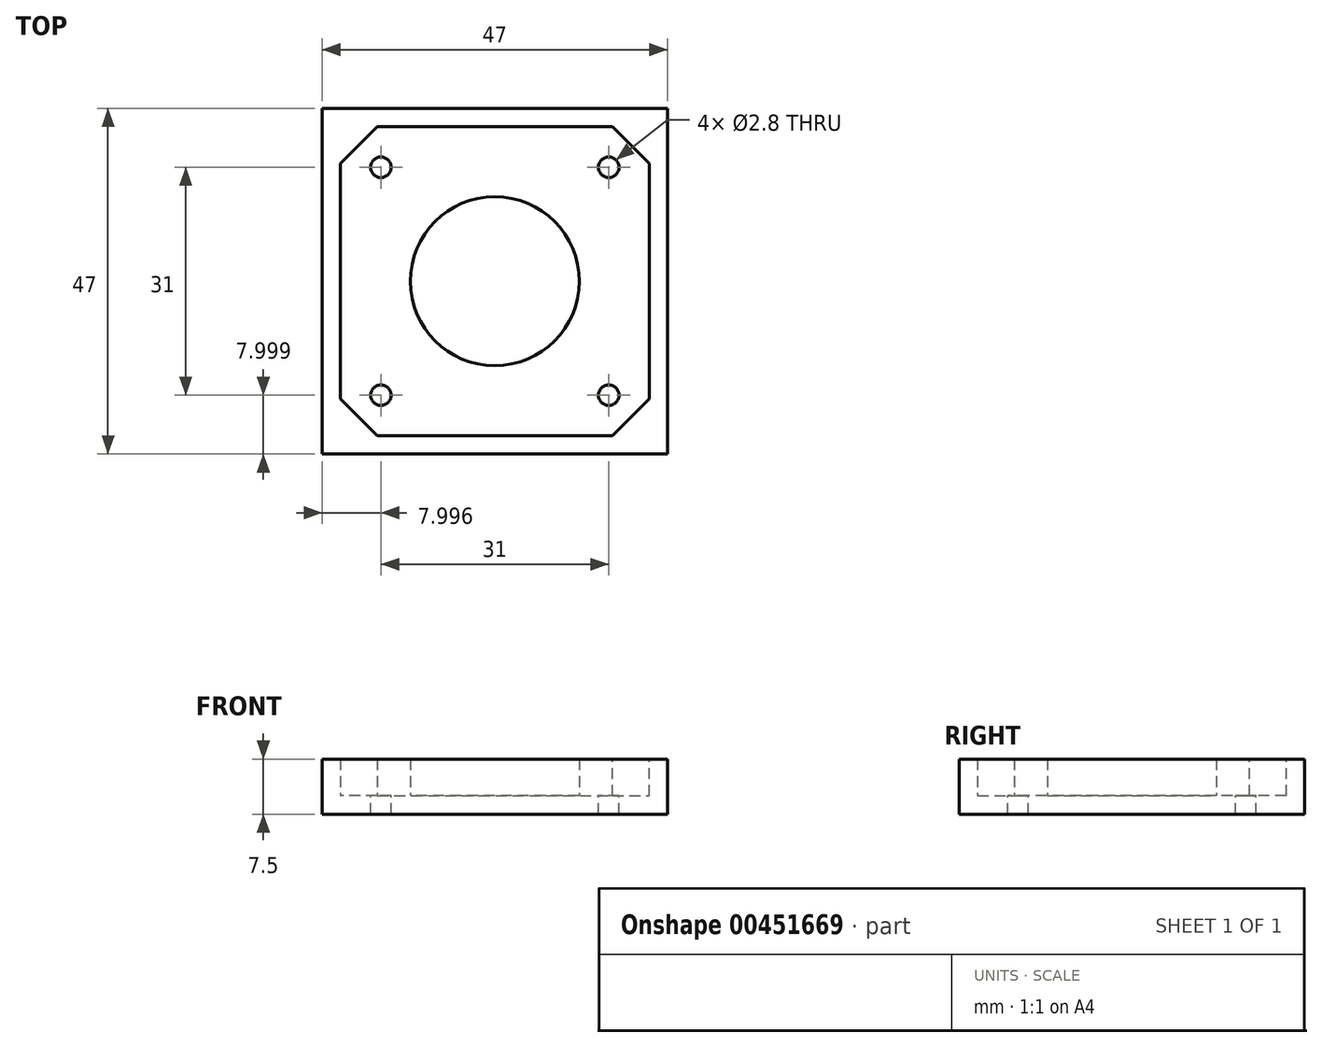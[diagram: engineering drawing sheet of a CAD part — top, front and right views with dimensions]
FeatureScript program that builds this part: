
annotation { "Feature Type Name" : "Feature", "Feature Type Description" : "" }
export const myFeature = defineFeature(function(context is Context, id is Id, definition is map)
    precondition{}
    {
        {
            var Q0;
            Q0=qCreatedBy(makeId("Top.planeOp"),FACE);
            var sketch = newSketch(context, id + "F0", { "sketchPlane" : qUnion([Q0])});
            skLineSegment(sketch, "E0.bottom", {"start": v(-41.82, 29.14) * mm, "end": v(0.18, 29.14) * mm});
            skLineSegment(sketch, "E0.top", {"start": v(-41.82, -12.86) * mm, "end": v(0.18, -12.86) * mm});
            skLineSegment(sketch, "E0.left", {"start": v(-41.82, 29.14) * mm, "end": v(-41.82, -12.86) * mm});
            skLineSegment(sketch, "E0.right", {"start": v(0.18, 29.14) * mm, "end": v(0.18, -12.86) * mm});
            skLineSegment(sketch, "E1", {"start": v(-41.82, 29.14) * mm, "end": v(0.18, -12.86) * mm, "construction": true});
            skCircle(sketch, "E2", {"center": v(-20.82, 8.14) * mm, "radius": 11.5 * mm});
            skLineSegment(sketch, "E3.bottom", {"start": v(-36.32, -7.36) * mm, "end": v(-5.32, -7.36) * mm, "construction": true});
            skLineSegment(sketch, "E3.top", {"start": v(-36.32, 23.64) * mm, "end": v(-5.32, 23.64) * mm, "construction": true});
            skLineSegment(sketch, "E3.left", {"start": v(-36.32, -7.36) * mm, "end": v(-36.32, 23.64) * mm, "construction": true});
            skLineSegment(sketch, "E3.right", {"start": v(-5.32, -7.36) * mm, "end": v(-5.32, 23.64) * mm, "construction": true});
            skCircle(sketch, "E4", {"center": v(-36.32, 23.64) * mm, "radius": 1.4 * mm});
            skCircle(sketch, "E5", {"center": v(-5.32, 23.64) * mm, "radius": 1.4 * mm});
            skCircle(sketch, "E6", {"center": v(-5.32, -7.36) * mm, "radius": 1.4 * mm});
            skCircle(sketch, "E7", {"center": v(-36.32, -7.36) * mm, "radius": 1.4 * mm});
            skSolve(sketch);
        }
        {
            var Q0;
            Q0=makeQuery(id+"F0.imprint","IMPRINT",FACE,{"disambiguationData":[TD([[makeQuery(id+"F0.imprint","IMPRINT",EDGE,{"derivedFrom":sQuery(id+"F0.wireOp",EDGE,"E2")}),1.0]])]});
            var Q1;
            Q1=makeQuery(id+"F0.imprint","IMPRINT",FACE,{"disambiguationData":[TD([[makeQuery(id+"F0.imprint","IMPRINT",EDGE,{"derivedFrom":sQuery(id+"F0.wireOp",EDGE,"E4")}),1.0]])]});
            var Q2;
            Q2=makeQuery(id+"F0.imprint","IMPRINT",FACE,{"disambiguationData":[TD([[makeQuery(id+"F0.imprint","IMPRINT",EDGE,{"derivedFrom":sQuery(id+"F0.wireOp",EDGE,"E5")}),1.0]])]});
            var Q3;
            Q3=makeQuery(id+"F0.imprint","IMPRINT",FACE,{"disambiguationData":[TD([[makeQuery(id+"F0.imprint","IMPRINT",EDGE,{"derivedFrom":sQuery(id+"F0.wireOp",EDGE,"E6")}),1.0]])]});
            var Q4;
            Q4=makeQuery(id+"F0.imprint","IMPRINT",FACE,{"disambiguationData":[TD([[makeQuery(id+"F0.imprint","IMPRINT",EDGE,{"derivedFrom":sQuery(id+"F0.wireOp",EDGE,"E7")}),1.0]])]});
            var Q5;
            Q5=makeQuery(id+"F0.imprint","IMPRINT",FACE,{"disambiguationData":[TD([[makeQuery(id+"F0.imprint","IMPRINT",EDGE,{"derivedFrom":sQuery(id+"F0.wireOp",EDGE,"E0.bottom")}),-1.0]])]});
            extrude(context, id + "F1", {"entities" : qUnion([Q0, Q1, Q2, Q3, Q4, Q5]), "depth" : 5 * mm});
        }
        {
            var Q0;
            Q0=makeQuery(id+"F1.opExtrude","CAP_FACE",FACE,{"disambiguationData":[OSD([sQuery(id+"F0.wireOp",EDGE,"E0.bottom"),sQuery(id+"F0.wireOp",EDGE,"E0.top"),sQuery(id+"F0.wireOp",EDGE,"E0.left"),sQuery(id+"F0.wireOp",EDGE,"E0.right"),sQuery(id+"F0.wireOp",EDGE,"E4"),sQuery(id+"F0.wireOp",EDGE,"E5"),sQuery(id+"F0.wireOp",EDGE,"E6"),sQuery(id+"F0.wireOp",EDGE,"E7")])],"isStart":false});
            shell(context, id + "F2", {"entities" : qUnion([Q0]), "thickness" : 2.5 * mm, "oppositeDirection" : true});
        }
        {
            var Q0;
            Q0=makeQuery(id+"F2.opShell","OFFSET_EDGE",EDGE,{"disambiguationData":[OSD([sQuery(id+"F0.wireOp",EDGE,"E0.bottom"),sQuery(id+"F0.wireOp",EDGE,"E0.left")])]});
            var Q1;
            Q1=makeQuery(id+"F2.opShell","OFFSET_EDGE",EDGE,{"disambiguationData":[OSD([sQuery(id+"F0.wireOp",EDGE,"E0.bottom"),sQuery(id+"F0.wireOp",EDGE,"E0.right")])]});
            var Q2;
            Q2=makeQuery(id+"F2.opShell","OFFSET_EDGE",EDGE,{"disambiguationData":[OSD([sQuery(id+"F0.wireOp",EDGE,"E0.top"),sQuery(id+"F0.wireOp",EDGE,"E0.right")])]});
            var Q3;
            Q3=makeQuery(id+"F2.opShell","OFFSET_EDGE",EDGE,{"disambiguationData":[OSD([sQuery(id+"F0.wireOp",EDGE,"E0.top"),sQuery(id+"F0.wireOp",EDGE,"E0.left")])]});
            chamfer(context, id + "F3", {"entities" : qUnion([Q0, Q1, Q2, Q3]), "width" : 5 * mm, "tangentPropagation" : true});
        }
        {
            var Q0;
            Q0=makeQuery(id+"F0.imprint","IMPRINT",FACE,{"disambiguationData":[TD([[makeQuery(id+"F0.imprint","IMPRINT",EDGE,{"derivedFrom":sQuery(id+"F0.wireOp",EDGE,"E2")}),1.0]])]});
            extrude(context, id + "F4", {"entities" : qUnion([Q0]), "operationType" : NewBodyOperationType.ADD, "depth" : 5 * mm});
        }
        {
            var Q0;
            Q0=makeQuery(id+"F0.imprint","IMPRINT",FACE,{"disambiguationData":[TD([[makeQuery(id+"F0.imprint","IMPRINT",EDGE,{"derivedFrom":sQuery(id+"F0.wireOp",EDGE,"E7")}),1.0]])]});
            var Q1;
            Q1=makeQuery(id+"F0.imprint","IMPRINT",FACE,{"disambiguationData":[TD([[makeQuery(id+"F0.imprint","IMPRINT",EDGE,{"derivedFrom":sQuery(id+"F0.wireOp",EDGE,"E4")}),1.0]])]});
            var Q2;
            Q2=makeQuery(id+"F0.imprint","IMPRINT",FACE,{"disambiguationData":[TD([[makeQuery(id+"F0.imprint","IMPRINT",EDGE,{"derivedFrom":sQuery(id+"F0.wireOp",EDGE,"E5")}),1.0]])]});
            var Q3;
            Q3=makeQuery(id+"F0.imprint","IMPRINT",FACE,{"disambiguationData":[TD([[makeQuery(id+"F0.imprint","IMPRINT",EDGE,{"derivedFrom":sQuery(id+"F0.wireOp",EDGE,"E6")}),1.0]])]});
            extrude(context, id + "F5", {"entities" : qUnion([Q0, Q1, Q2, Q3]), "operationType" : NewBodyOperationType.REMOVE, "oppositeDirection" : true, "depth" : 25 * mm});
        }
    });
